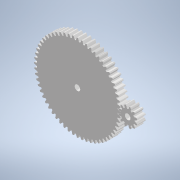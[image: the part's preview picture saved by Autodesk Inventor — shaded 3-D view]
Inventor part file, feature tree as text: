
AUTODESK INVENTOR PART (.ipt)
format: ipt  version: 2022 (Build 260153000, 153)  size: 4,260,352 bytes
history: native  units: mm
features: extrude x4, sketch x2
ambient origin geometry x8: Origin, YZ Plane, XZ Plane, XY Plane, X Axis, Y Axis, Z Axis, Center Point
bodies: Solid1 (feature_tree)
feature tree (6):
  sketch  "Sketch1"  dims[d0=3.0mm d1=60.0mm d3=360.0deg]
  sketch  "Sketch2"  dims[d5=3.0mm d6=60.0mm d8=360.0deg d10=6.2mm d11=0.0mm d14=6.2mm d15=0.0mm d16=6.0mm d17=0.0mm d18=0.3mm d20=0.3mm d21=6.0mm d22=0.0mm]
  extrude  "Extrusion1"  Depth=60.0mm TaperAngle=360.0deg
  extrude  "Extrusion3"  Depth=6.0mm TaperAngle=360.0deg
  extrude  "Extrusion4"  Depth=6.0mm TaperAngle=0.0deg
  extrude  "Extrusion5"  Depth=6.0mm TaperAngle=0.0deg
